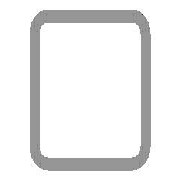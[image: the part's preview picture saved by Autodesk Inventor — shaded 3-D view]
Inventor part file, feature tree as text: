
AUTODESK INVENTOR PART (.ipt)
format: ipt  version: 2025.1 (Build 291241020, 241B)  size: 134,656 bytes
history: native  units: mm (DEFAULTED — no unit token found)
features: other x4, sketch x1, plane x1
ambient origin geometry x8: Origin, YZ Plane, XZ Plane, XY Plane, X Axis, Y Axis, Z Axis, Center Point
bodies: Solid1 (feature_tree), Body (feature_tree)
feature tree (6):
  parser-record x1  (decoder bookkeeping rows leaked as tree rows — omitted from the tree; the rows remain in map.json)
  other  "Driven Length"
  other  "Start Plane"
  other  "End Plane"
  sketch  "Sketch3"  dims[d3=1050.0mm d4=0.0mm d7=8.0mm d9=100.0mm d11=100.0mm d12=4.0mm d13=100.0mm d14=1150.0mm d15=50.0mm d16=50.0mm d17=90.0deg d18=1050.0mm]
  plane  "Work Plane3"
